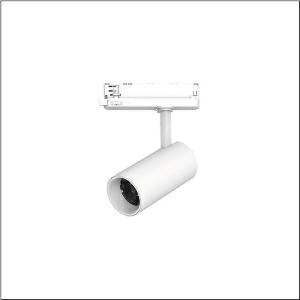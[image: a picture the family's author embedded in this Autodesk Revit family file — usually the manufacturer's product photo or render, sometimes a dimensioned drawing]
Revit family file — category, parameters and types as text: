
# Revit family: spot_31_slim_51sf127fa1b
name_source: partatom
category: Lighting Fixtures
units: mm (PartAtom-declared; Revit-internal decimal feet)

## family parameters
Cut with Voids When Loaded = No
Host = Face
Light Source = No
Part Type = Normal
Room Calculation Point = No
Round Connector Dimension = Use Diameter
Shared = No

## types (1)
- Spot 31 Slim (1 x LED, 2090 lm, 16.3 W, 2700K)
    Apparent Load = 16 VA
    CIE Flux Codes = 94 98 99 100 100
    Color Rendering = 90
    Color Temperature = 2700K
    Default Elevation = 1800 mm
    Description = Spot 31 Slim, directional spotlight, light control with reflector, of aluminium, LED rated luminous flux: 2.100lm, light colour: 927, control gear: ECG, with 3-phase adapter, mains connection: 220..240V, AC, 50/60Hz, housing, of aluminium, traffic white (RAL 9016), diameter: 70mm, adapter, of plastic, protection rating (complete): IP20, insulation class (complete): insulation class I (protective earthing), certification: CE, impact resistance: IK02, packaging unit: 1 piece
    Height = 210 mm
    Lamp = 1 x LED
    Lamp Light Flux = 2090 lm
    Lamp Power = 16.3 W
    Lamp count = 1
    Length = 70 mm
    Luminous efficacy = 128 lm/W
    Manufacturer = Siteco
    ModVariant = No
    Model = 51SF127FA1B
    Mounting Place = Ceiling
    Mounting Type = Pendant
    Number of Poles = 1
    OnlyDefault = Yes
    Power Factor = 1
    Product Name = Spot 31 Slim
    Product group = directional spotlight
    ProductGroupID = 905
    Protection Class = Protection class I
    Protection Degree = IP 20
    RLX_Detail_Level = 1
    RLX_Emergency_Light_Flux = 0 lm
    RLX_Emergency_Type = 0
    RLX_Emergency_Type_DB = No
    RlxData = <blob elided: 13517 chars, md5=c9aa887c>
    Socket = socket
    Standby Power = 0 W
    System Light Flux = 2090 lm
    System Power = 16 W
    Type Comments = Product without accessories
    Type Image = l_1228470.jpg
    URL = http://relux.com
    VarID = ---
    Voltage = 0 V
    Weight = 0.00 kg
    Width = 0 mm  [stored 0 ft]

note: [stored X ft] marks values corroborated as IEEE doubles in the binary element streams (Revit-internal decimal feet)

## geometry (parser evidence)
native form markers: Sweep x9
no freeform markers — native parametric forms only
